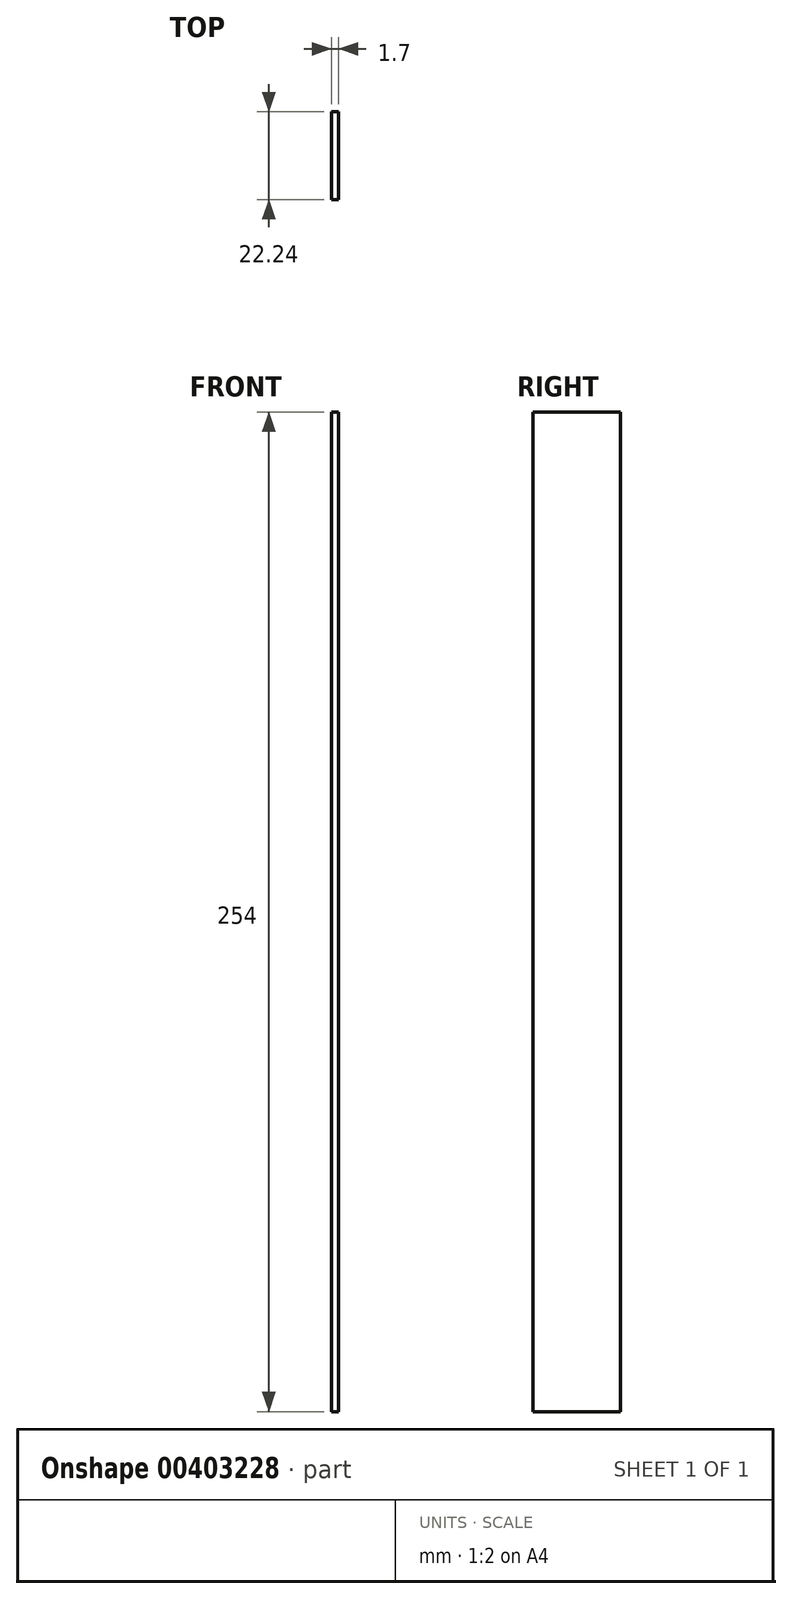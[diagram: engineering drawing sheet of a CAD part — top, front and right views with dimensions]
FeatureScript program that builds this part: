
annotation { "Feature Type Name" : "Feature", "Feature Type Description" : "" }
export const myFeature = defineFeature(function(context is Context, id is Id, definition is map)
    precondition{}
    {
        {
            var Q0;
            Q0=qCreatedBy(makeId("Right.planeOp"),FACE);
            var sketch = newSketch(context, id + "F0", { "sketchPlane" : qUnion([Q0])});
            skLineSegment(sketch, "E0.bottom", {"start": v(11.13, -127) * mm, "end": v(-11.12, -127) * mm});
            skLineSegment(sketch, "E0.top", {"start": v(11.13, 127) * mm, "end": v(-11.12, 127) * mm});
            skLineSegment(sketch, "E0.left", {"start": v(11.13, -127) * mm, "end": v(11.13, 127) * mm});
            skLineSegment(sketch, "E0.right", {"start": v(-11.12, -127) * mm, "end": v(-11.12, 127) * mm});
            skPoint(sketch, "E0.middle", {"position": v(0, 0) * mm});
            skSolve(sketch);
        }
        {
            var Q0;
            Q0=makeQuery(id+"F0.imprint","IMPRINT",FACE,{"disambiguationData":[TD([[makeQuery(id+"F0.imprint","IMPRINT",EDGE,{"derivedFrom":sQuery(id+"F0.wireOp",EDGE,"E0.bottom")}),-1.0]])]});
            extrude(context, id + "F1", {"entities" : qUnion([Q0]), "depth" : 1.7 * mm});
        }
    });
